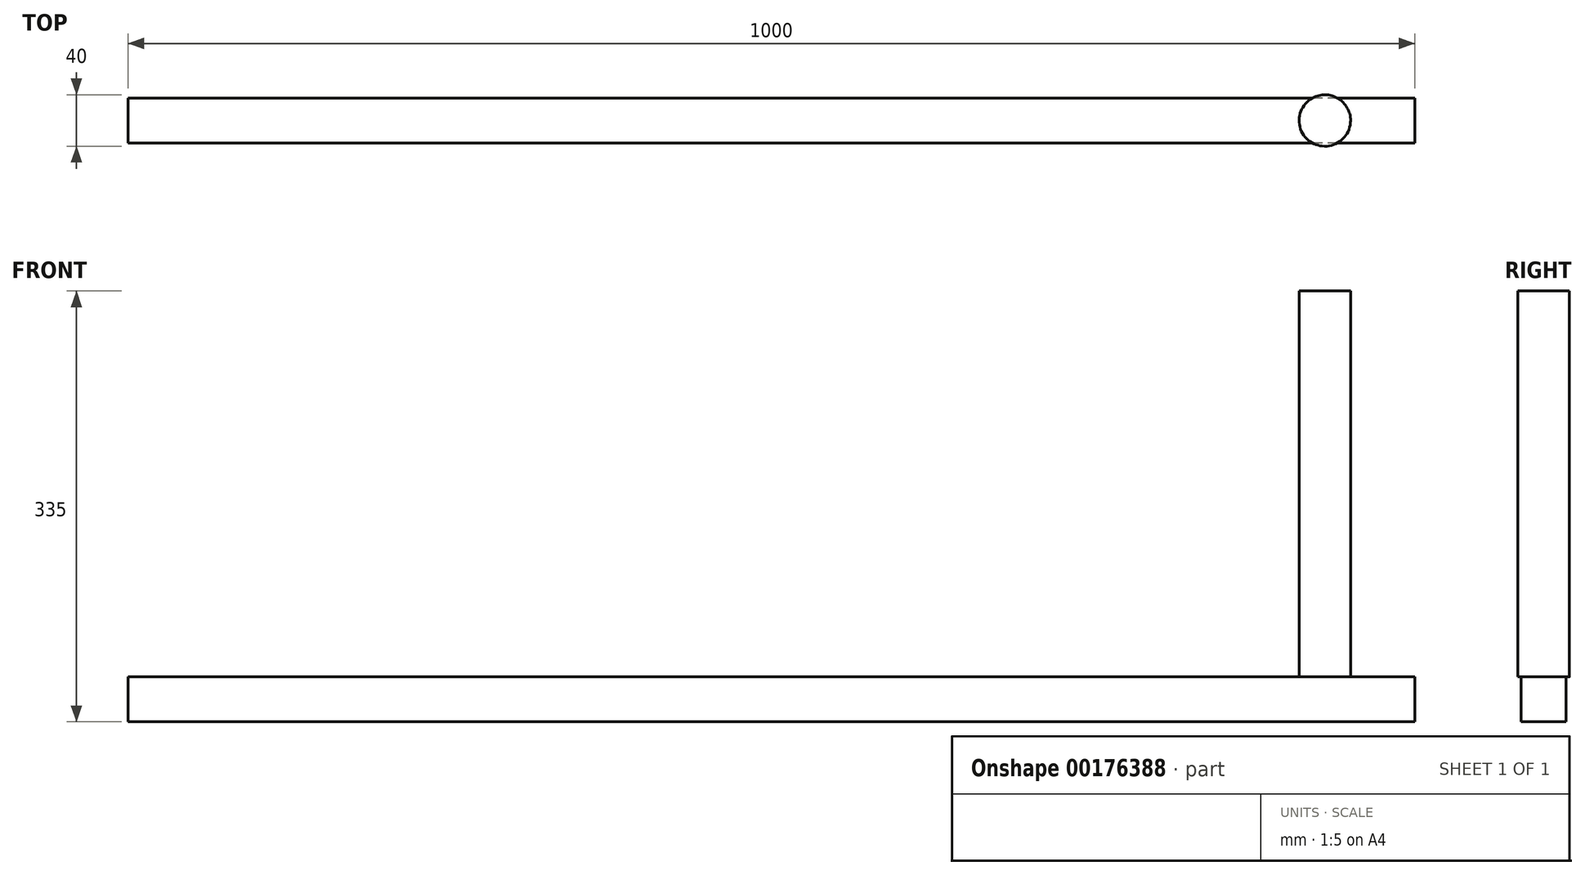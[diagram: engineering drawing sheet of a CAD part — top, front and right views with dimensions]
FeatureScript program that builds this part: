
annotation { "Feature Type Name" : "Feature", "Feature Type Description" : "" }
export const myFeature = defineFeature(function(context is Context, id is Id, definition is map)
    precondition{}
    {
        {
            var Q0;
            Q0=qCreatedBy(makeId("Front.planeOp"),FACE);
            var sketch = newSketch(context, id + "F0", { "sketchPlane" : qUnion([Q0])});
            skLineSegment(sketch, "E0", {"start": v(0, 0) * mm, "end": v(-1000, 0) * mm});
            skLineSegment(sketch, "E1", {"start": v(0, 0) * mm, "end": v(0, 35) * mm});
            skLineSegment(sketch, "E2", {"start": v(0, 35) * mm, "end": v(-1000, 35) * mm});
            skLineSegment(sketch, "E3", {"start": v(-1000, 35) * mm, "end": v(-1000, 0) * mm});
            skSolve(sketch);
        }
        {
            var Q0;
            Q0=makeQuery(id+"F0.imprint","IMPRINT",FACE,{"disambiguationData":[TD([[makeQuery(id+"F0.imprint","IMPRINT",EDGE,{"derivedFrom":sQuery(id+"F0.wireOp",EDGE,"E0")}),-1.0]])]});
            extrude(context, id + "F1", {"entities" : qUnion([Q0]), "oppositeDirection" : true, "depth" : 35 * mm});
        }
        {
            var Q0;
            Q0=makeQuery(id+"F1.opExtrude","SWEPT_FACE",FACE,{"disambiguationData":[OSD([sQuery(id+"F0.wireOp",EDGE,"E2")])]});
            var sketch = newSketch(context, id + "F2", { "sketchPlane" : qUnion([Q0])});
            skCircle(sketch, "E4", {"center": v(-70, 17.5) * mm, "radius": 20 * mm});
            skLineSegment(sketch, "E5", {"start": v(-70, 17.5) * mm, "end": v(0, 17.5) * mm, "construction": true});
            skSolve(sketch);
        }
        {
            var Q0;
            Q0 = qSketchRegion(id + "F2", true);
            extrude(context, id + "F3", {"entities" : qUnion([Q0]), "operationType" : NewBodyOperationType.ADD, "depth" : 300 * mm});
        }
    });
